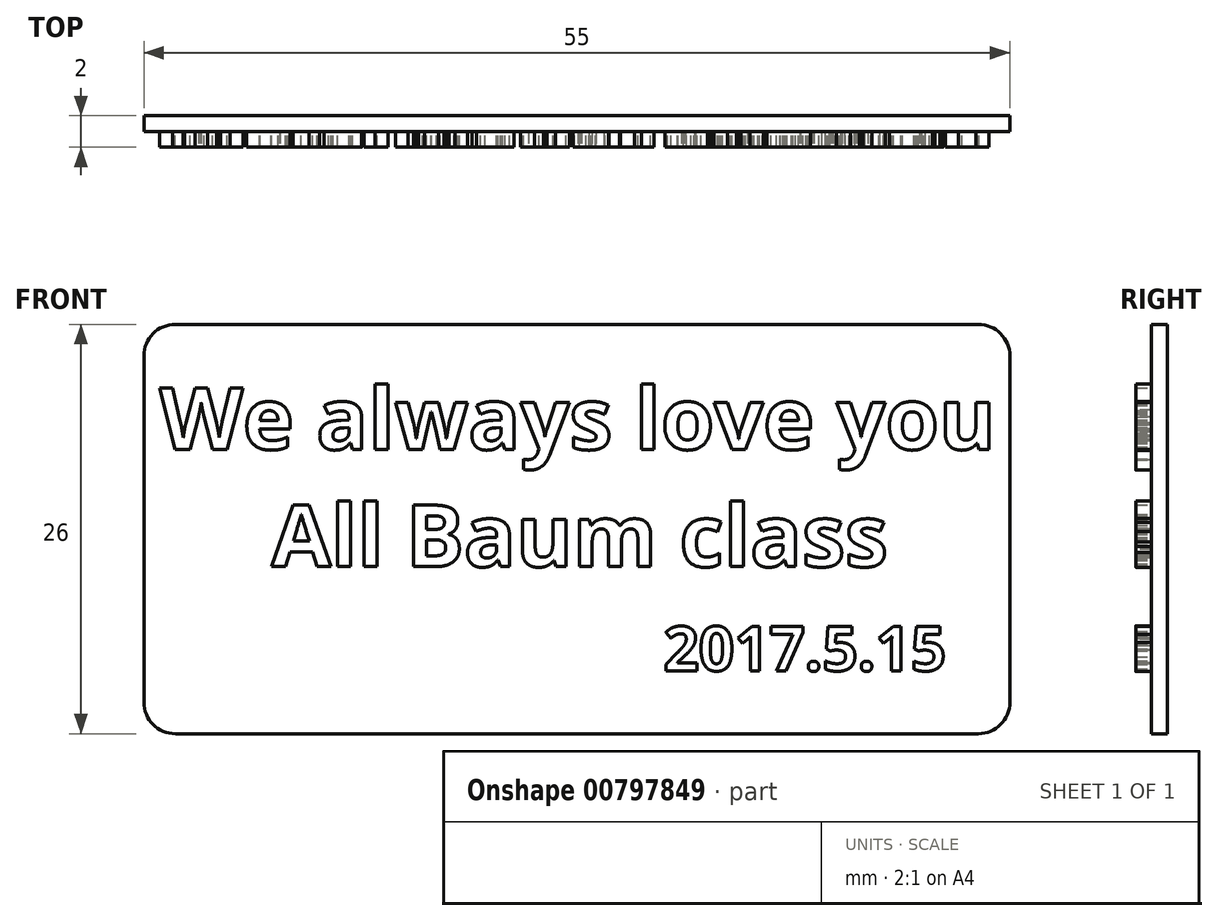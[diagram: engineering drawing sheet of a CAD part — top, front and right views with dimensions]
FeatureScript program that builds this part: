
annotation { "Feature Type Name" : "Feature", "Feature Type Description" : "" }
export const myFeature = defineFeature(function(context is Context, id is Id, definition is map)
    precondition{}
    {
        {
            var Q0;
            Q0=qCreatedBy(makeId("Front.planeOp"),FACE);
            var sketch = newSketch(context, id + "F0", { "sketchPlane" : qUnion([Q0])});
            skLineSegment(sketch, "E0.bottom", {"start": v(27.5, 13) * mm, "end": v(-27.5, 13) * mm});
            skLineSegment(sketch, "E0.top", {"start": v(27.5, -13) * mm, "end": v(-27.5, -13) * mm});
            skLineSegment(sketch, "E0.left", {"start": v(27.5, 13) * mm, "end": v(27.5, -13) * mm});
            skLineSegment(sketch, "E0.right", {"start": v(-27.5, 13) * mm, "end": v(-27.5, -13) * mm});
            skPoint(sketch, "E0.middle", {"position": v(0, 0) * mm});
            skSolve(sketch);
        }
        {
            var Q0;
            Q0 = qSketchRegion(id + "F0", true);
            extrude(context, id + "F1", {"entities" : qUnion([Q0]), "depth" : 1 * mm, "offsetDistance" : 25 * mm});
        }
        {
            var Q0;
            Q0=makeQuery(id+"F1.opExtrude","CAP_FACE",FACE,{"disambiguationData":[OSD([sQuery(id+"F0.wireOp",EDGE,"E0.bottom"),sQuery(id+"F0.wireOp",EDGE,"E0.top"),sQuery(id+"F0.wireOp",EDGE,"E0.left"),sQuery(id+"F0.wireOp",EDGE,"E0.right")])],"isStart":false});
            var sketch = newSketch(context, id + "F2", { "sketchPlane" : qUnion([Q0])});
            skText(sketch, "E1", { "text": "We always love you\n     All Baum class", "fontName": "OpenSans-Bold.ttf"});
            skText(sketch, "E2", { "text": "2017.5.15", "fontName": "OpenSans-Bold.ttf"});
            const initialGuessF2  = {"E1": [-0.0265, 0.00506, 1, 0, 0.00394], "E2": [0.0055, -0.009, 1, 0, 0.00283]};
            skSetInitialGuess(sketch, initialGuessF2);
            skSolve(sketch);
        }
        {
            var Q0;
            Q0 = qSketchRegion(id + "F2", true);
            extrude(context, id + "F3", {"entities" : qUnion([Q0]), "operationType" : NewBodyOperationType.ADD, "depth" : 1 * mm, "offsetDistance" : 25 * mm});
        }
        {
            var Q0;
            Q0=makeQuery(id+"F1.opExtrude","SWEPT_EDGE",EDGE,{"disambiguationData":[OSD([sQuery(id+"F0.wireOp",EDGE,"E0.bottom"),sQuery(id+"F0.wireOp",EDGE,"E0.right")])]});
            var Q1;
            Q1=makeQuery(id+"F1.opExtrude","SWEPT_EDGE",EDGE,{"disambiguationData":[OSD([sQuery(id+"F0.wireOp",EDGE,"E0.top"),sQuery(id+"F0.wireOp",EDGE,"E0.right")])]});
            var Q2;
            Q2=makeQuery(id+"F1.opExtrude","SWEPT_EDGE",EDGE,{"disambiguationData":[OSD([sQuery(id+"F0.wireOp",EDGE,"E0.bottom"),sQuery(id+"F0.wireOp",EDGE,"E0.left")])]});
            var Q3;
            Q3=makeQuery(id+"F1.opExtrude","SWEPT_EDGE",EDGE,{"disambiguationData":[OSD([sQuery(id+"F0.wireOp",EDGE,"E0.top"),sQuery(id+"F0.wireOp",EDGE,"E0.left")])]});
            fillet(context, id + "F4", {"entities" : qUnion([Q0, Q1, Q2, Q3]), "radius" : 2 * mm, "tangentPropagation" : true, "allowEdgeOverflow" : false});
        }
    });
